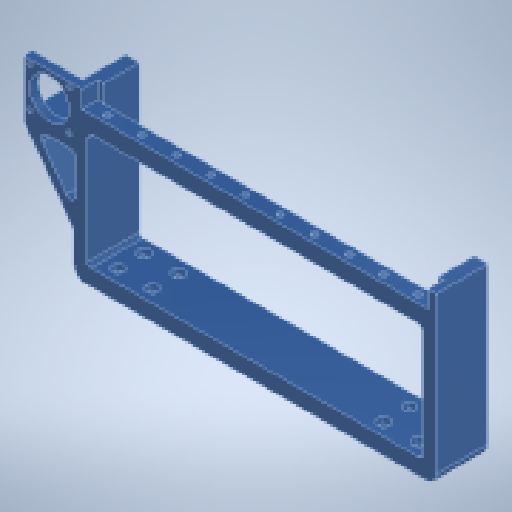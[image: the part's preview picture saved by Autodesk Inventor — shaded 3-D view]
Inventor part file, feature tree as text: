
AUTODESK INVENTOR PART (.ipt)
format: ipt  version: 2024.1 (Build 281209000, 209)  size: 447,488 bytes
history: native  units: in
note: dims shown in document units (in); Inventor stores cm internally (conversion verified against a paired STEP export)
features: extrude x12, sketch x12, fillet x5, chamfer x2
ambient origin geometry x8: Origin, YZ Plane, XZ Plane, XY Plane, X Axis, Y Axis, Z Axis, Center Point
bodies: Solid1 (feature_tree)
feature tree (31):
  extrude  "Extrusion1"  Depth=1.1811in
  extrude  "Extrusion2"  Depth=0.315in
  extrude  "Extrusion3"  Depth=1.1811in
  chamfer  "Chamfer1"  Distance=3.4252in
  fillet  "Fillet1"  Radius=0.122in
  fillet  "Fillet2"  Radius=0.122in
  extrude  "Extrusion4"  Depth=0.122in
  extrude  "Extrusion5"  Depth=0.122in
  extrude  "Extrusion6"  Depth=0.122in
  chamfer  "Chamfer2"  Distance=0.3937in
  extrude  "Extrusion7"  Depth=0.3937in
  extrude  "Extrusion8"  Depth=0.4528in
  extrude  "Extrusion9"  Depth=0.4528in
  fillet  "Fillet4"  Radius=0.3937in
  extrude  "Extrusion10"  Depth=0.3937in
  extrude  "Extrusion11"  Depth=0.4528in
  fillet  "Fillet5"  Radius=0.7874in
  fillet  "Fillet6"  Radius=0.5906in
  extrude  "Extrusion12"  Depth=0.7874in
  sketch  "Sketch1"  dims[d0=8.2677in d1=1.1811in]
  sketch  "Sketch2"  dims[d2=0.374in d3=0.0in d4=0.315in]
  sketch  "Sketch3"  dims[d5=0.315in d6=1.1811in d7=3.4252in d8=0.0in d9=0.122in d10=0.122in]
  sketch  "Sketch4"  dims[d11=0.122in d12=0.122in]
  sketch  "Sketch5"  dims[d13=0.122in d14=0.122in]
  sketch  "Sketch6"  dims[d15=0.122in d16=0.122in]
  sketch  "Sketch7"  dims[d17=0.7874in]
  sketch  "Sketch8"  dims[d18=0.5906in]
  sketch  "Sketch9"  dims[d19=0.7874in]
  sketch  "Sketch10"  dims[d20=0.5906in]
  sketch  "Sketch11"  dims[d21=0.2953in]
  sketch  "Sketch12"  dims[d22=0.2953in d23=0.3937in d24=0.3937in d25=0.2953in d26=0.2953in d27=0.3937in d28=0.3937in d29=0.5906in d30=0.7874in d31=0.5906in d32=0.7874in d33=0.0in d34=0.0in d35=0.0787in d36=0.0787in d37=45.0deg d38=0.0787in d39=0.2362in d40=0.3937in d41=0.3937in d42=0.3543in d43=0.0in d44=0.126in d45=0.3622in d46=0.126in d47=0.3622in d48=0.3543in d49=0.0in d50=0.1024in d51=0.1772in d52=0.4016in d53=3.937in d55=0.7874in d56=0.3937in d58=0.3937in d60=0.3937in d61=0.0in d62=0.0197in d63=0.0787in d64=45.0deg d65=0.1969in d66=1.2992in d67=1.1417in d68=0.0in d69=0.189in d70=1.1417in d71=0.0in d72=0.9055in d73=0.5551in d74=0.5551in d75=0.0in d76=0.0in d78=0.1181in d79=1.5748in d80=0.3937in d81=0.0in d82=0.189in d83=0.2756in d85=0.9055in d86=0.0in d87=0.0in d88=0.1181in d89=0.2362in d90=0.1024in d91=0.1024in d92=0.1024in d93=0.1024in d94=0.4528in d95=0.4528in d96=0.4528in d97=0.4528in d98=0.4528in d99=0.4528in d100=0.4528in d101=0.4528in d102=0.0in d103=0.0in]
